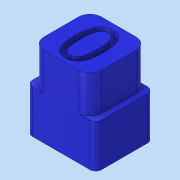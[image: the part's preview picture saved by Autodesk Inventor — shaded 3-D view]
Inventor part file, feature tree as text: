
AUTODESK INVENTOR PART (.ipt)
format: ipt  version: 2018 (Build 220112000, 112)  size: 177,664 bytes
history: native  units: mm
features: sketch x3, extrude x2, fillet x2, other x1, projected_geometry x1
ambient origin geometry x8: Origin, YZ Plane, XZ Plane, XY Plane, X Axis, Y Axis, Z Axis, Center Point
bodies: Volumenkörper1 (feature_tree)
feature tree (9):
  extrude  "Extrusion1"  Depth=10.0mm
  extrude  "Extrusion2"  Depth=10.0mm
  fillet  "Rundung1"  Radius=10.0mm
  fillet  "Rundung2"  Radius=6.5mm
  other  "Prägen1"
  sketch  "Skizze1"  dims[d0=12.0mm d1=10.0mm]
  sketch  "Skizze2"  dims[d2=14.0mm d3=0.0mm d4=10.0mm d5=10.0mm d6=6.5mm d7=0.0mm]
  sketch  "Skizze3"  dims[d8=2.0mm d9=1.0mm d10=1.0mm d11=1.0mm d12=1.0mm d13=3.490659mm]
  projected_geometry  "Projizierte Kontur1"
